# Revit family: QF_COMENDA_640251
name_source: partatom
category: Attrezzature speciali
units: mm (PartAtom-declared; Revit-internal decimal feet)

## family parameters
Basato su piano di lavoro = No
Condiviso = No
Numero OmniClass = 23.40.40.14
Punto di calcolo locali = No
Quota connettore circolare = Usa diametro
Sempre verticale = Sì
Taglio con vuoti quando caricato = No
Tipo di parte = Normale
Titolo OmniClass = Food Service Equipment

## types (1)
- 640251
    Altezza = 480 mm  [stored 1.5748 ft]
    Codice assieme = E1090320
    Descrizione = CS05 SOFTENER - 406L TREATED VOLUME AT 40° F - TO BE COMBINED WITH PRIME, HI-LINE MODELS
    Fase = 1
    Frequenza = 50 Hz
    Lunghezza = 200 mm  [stored 0.656168 ft]
    Modello = 640251
    Numero dei poli = 1
    Peso netto = 8.00 kg
    Pessione minima acqua fredda = 1800.0 Pa
    Potenza elettrica = 10 W
    Pressione massima acqua fredda = 5000.0 Pa
    Produttore = COMENDA
    Profondità = 400 mm  [stored 1.31234 ft]
    Temperatura raccomandata per acqua fredda = 20 °C
    Tensione = 230 V
    URL = www.comenda.eu
    URL catalogo = https://www.comenda.eu

note: [stored X ft] marks values corroborated as IEEE doubles in the binary element streams (Revit-internal decimal feet)

## geometry (parser evidence)
native form markers: Sweep x3
no freeform markers — native parametric forms only
